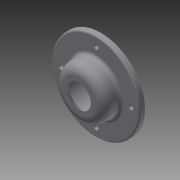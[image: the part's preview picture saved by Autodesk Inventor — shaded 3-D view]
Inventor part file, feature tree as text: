
AUTODESK INVENTOR PART (.ipt)
format: ipt  version: 2014 SP2 (Build 180246200, 246)  size: 158,208 bytes
history: native  units: mm
features: extrude x4, sketch x4, fillet x3, chamfer x1
ambient origin geometry x8: Origin, YZ Plane, XZ Plane, XY Plane, X Axis, Y Axis, Z Axis, Center Point
bodies: Solid1 (feature_tree)
feature tree (12):
  extrude  "Extrusion1"  Depth=28.5mm
  extrude  "Extrusion2"  Depth=13.5mm
  extrude  "Extrusion3"  Depth=3.0mm
  chamfer  "Chamfer2"  Distance=8.0mm
  fillet  "Fillet1"  Radius=50.5mm
  fillet  "Fillet2"  Radius=3.0mm
  fillet  "Fillet3"  Radius=5.0mm
  extrude  "Extrusion4"  Depth=2.0mm
  sketch  "Sketch1"  dims[d0=22.5mm d1=28.5mm]
  sketch  "Sketch2"  dims[d2=60.0mm d3=13.5mm]
  sketch  "Sketch3"  dims[d4=4.5mm d5=0.0mm d6=22.5mm d7=8.0mm d8=0.0mm d9=50.5mm d10=3.0mm d11=0.0mm]
  sketch  "Sketch5"  dims[d15=4.5mm d16=2.0mm d17=45.0deg d18=5.0mm d19=2.0mm d20=1.0mm d21=3.0mm d22=20.0mm d23=3.0mm d24=20.0mm d25=3.0mm d26=20.0mm d27=3.0mm d28=20.0mm d29=11.0mm d30=0.0mm]
